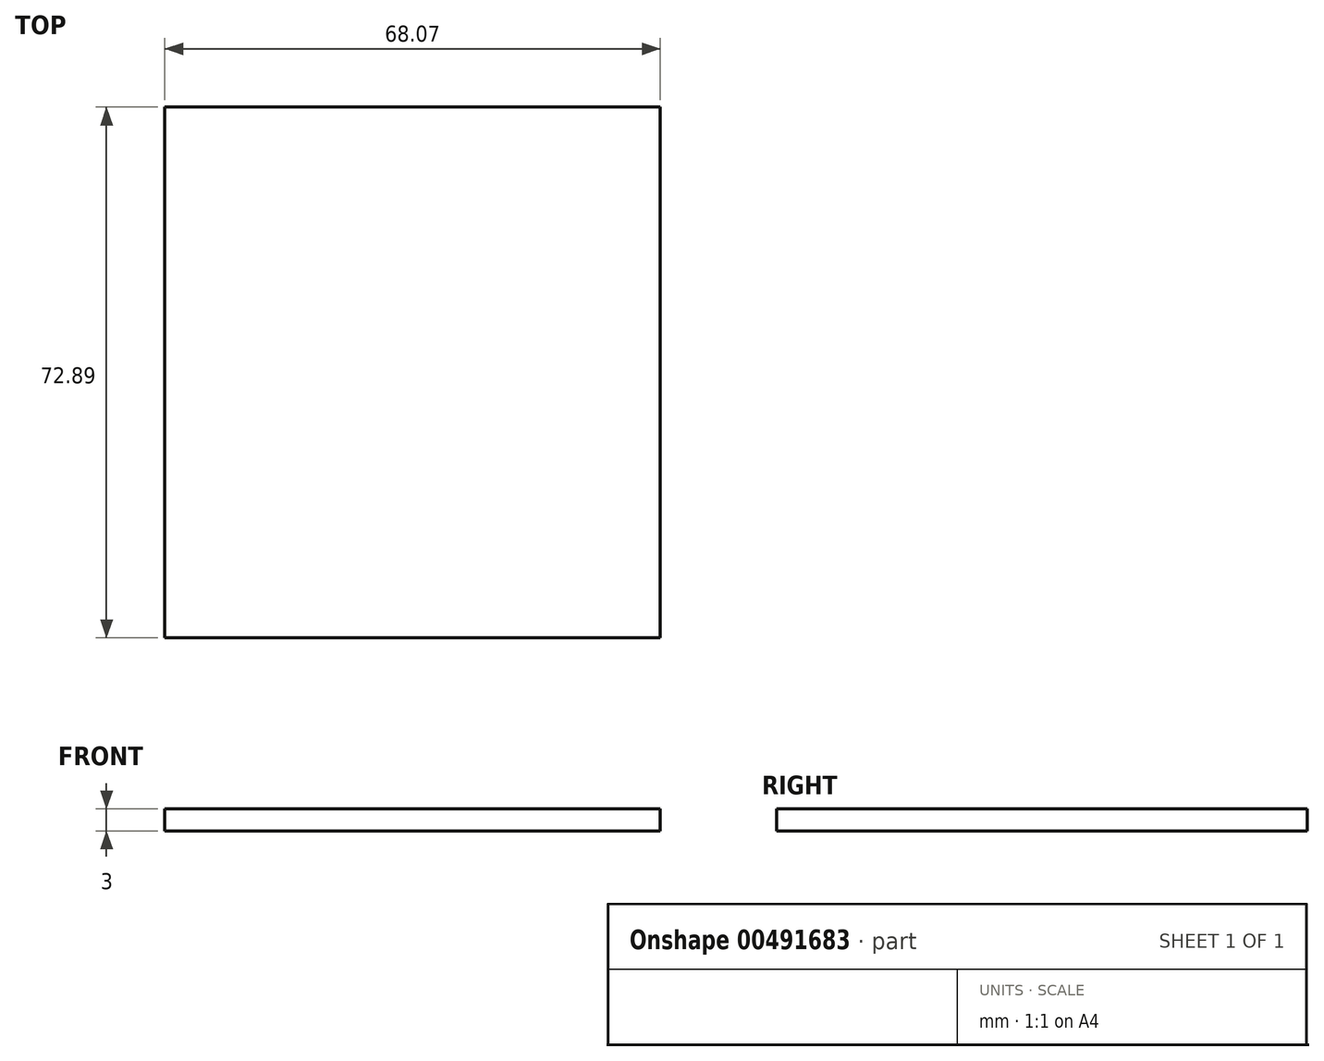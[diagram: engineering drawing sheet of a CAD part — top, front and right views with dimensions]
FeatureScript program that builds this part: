
annotation { "Feature Type Name" : "Feature", "Feature Type Description" : "" }
export const myFeature = defineFeature(function(context is Context, id is Id, definition is map)
    precondition{}
    {
        {
            var Q0;
            Q0=qCreatedBy(makeId("Top.planeOp"),FACE);
            var sketch = newSketch(context, id + "F0", { "sketchPlane" : qUnion([Q0])});
            skLineSegment(sketch, "E0.bottom", {"start": v(-35.79, 40.1) * mm, "end": v(32.28, 40.1) * mm});
            skLineSegment(sketch, "E0.top", {"start": v(-35.79, -32.8) * mm, "end": v(32.28, -32.8) * mm});
            skLineSegment(sketch, "E0.left", {"start": v(-35.79, 40.1) * mm, "end": v(-35.79, -32.8) * mm});
            skLineSegment(sketch, "E0.right", {"start": v(32.28, 40.1) * mm, "end": v(32.28, -32.8) * mm});
            skSolve(sketch);
        }
        {
            var Q0;
            Q0 = qSketchRegion(id + "F0", true);
            extrude(context, id + "F1", {"entities" : qUnion([Q0]), "depth" : 3 * mm});
        }
    });
